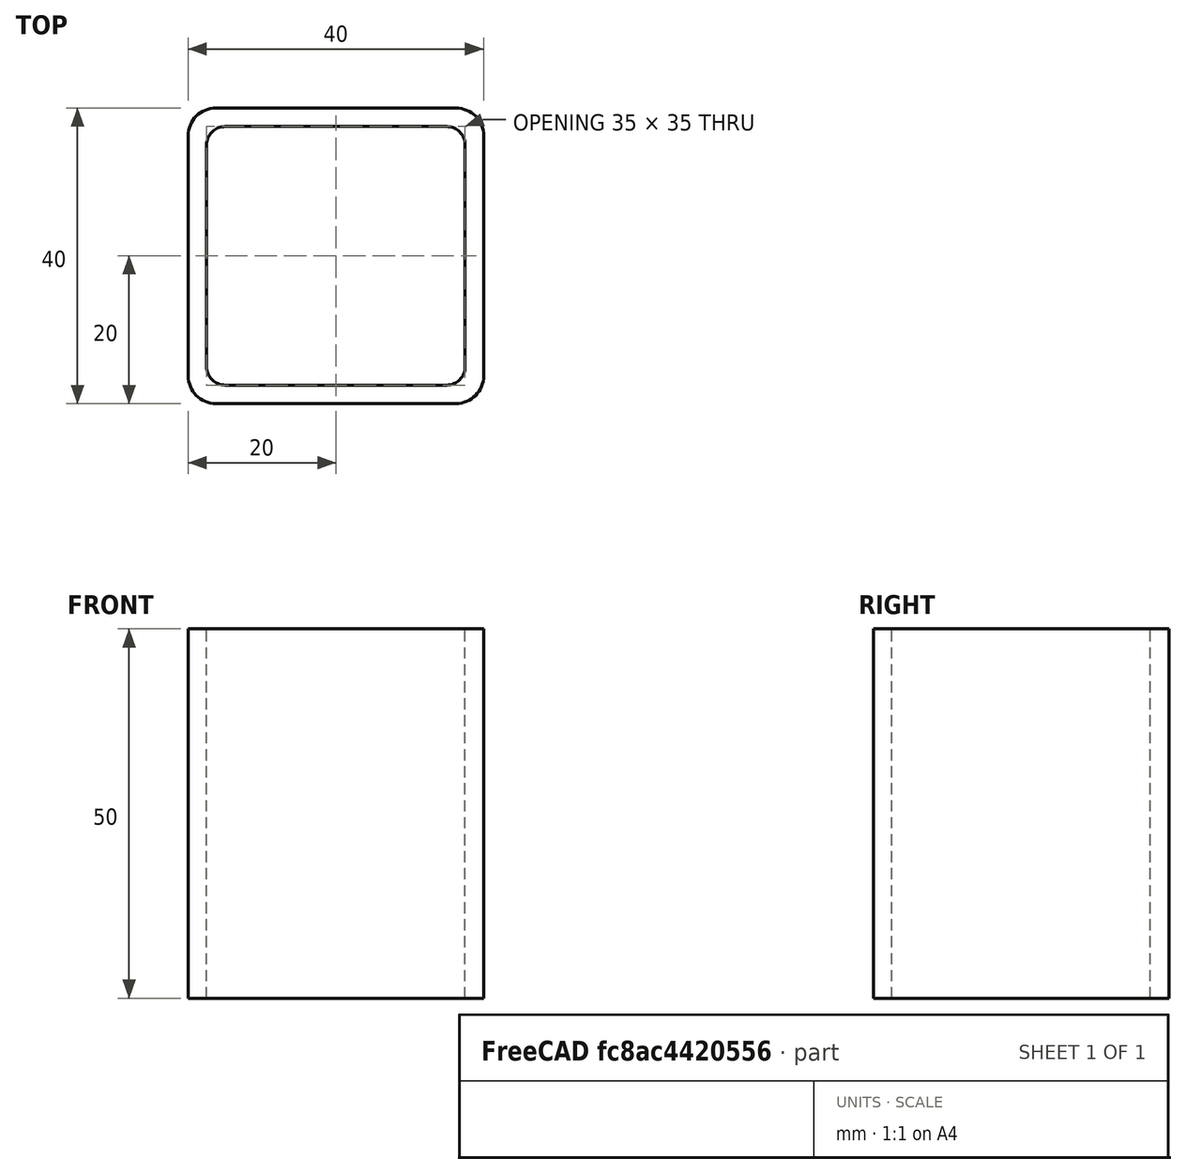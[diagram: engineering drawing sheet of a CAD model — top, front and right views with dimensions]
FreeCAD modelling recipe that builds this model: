
FCSTD DOCUMENT  (FreeCAD 0.15R4671 (Git))
Label: Square hollow section 40x40x2.5 EN10219 S235JRH
License: All rights reserved
LicenseURL: http://en.wikipedia.org/wiki/All_rights_reserved
objects: Sketcher::SketchObject×1, Part::Extrusion×1
note: 2 computed .brp shape members not serialized (recipe doc carries the construction recipe); baked Part::Feature solids carry a one-line shape summary decoded from their .brp

FEATURE [Sketcher::SketchObject] Sketch
  sketch-geometry (16):
    g0: LineSegment StartX=-15 StartY=17.5 StartZ=0 EndX=15 EndY=17.5 EndZ=0
    g1: LineSegment StartX=17.5 StartY=15 StartZ=0 EndX=17.5 EndY=-15 EndZ=0
    g2: LineSegment StartX=15 StartY=-17.5 StartZ=0 EndX=-15 EndY=-17.5 EndZ=0
    g3: LineSegment StartX=-17.5 StartY=-15 StartZ=0 EndX=-17.5 EndY=15 EndZ=0
    g4: LineSegment StartX=-16.25 StartY=20 StartZ=0 EndX=16.25 EndY=20 EndZ=0
    g5: LineSegment StartX=20 StartY=16.25 StartZ=0 EndX=20 EndY=-16.25 EndZ=0
    g6: LineSegment StartX=16.25 StartY=-20 StartZ=0 EndX=-16.25 EndY=-20 EndZ=0
    g7: LineSegment StartX=-20 StartY=-16.25 StartZ=0 EndX=-20 EndY=16.25 EndZ=0
    g8: ArcOfCircle CenterX=-15 CenterY=15 CenterZ=0 NormalX=0 NormalY=0 NormalZ=1 Radius=2.5 StartAngle=1.5708 EndAngle=3.14159
    g9: ArcOfCircle CenterX=15 CenterY=15 CenterZ=0 NormalX=0 NormalY=0 NormalZ=1 Radius=2.5 StartAngle=0 EndAngle=1.5708
    g10: ArcOfCircle CenterX=15 CenterY=-15 CenterZ=0 NormalX=0 NormalY=0 NormalZ=1 Radius=2.5 StartAngle=4.71239 EndAngle=6.28319
    g11: ArcOfCircle CenterX=-15 CenterY=-15 CenterZ=0 NormalX=0 NormalY=0 NormalZ=1 Radius=2.5 StartAngle=3.14159 EndAngle=4.71239
    g12: ArcOfCircle CenterX=16.25 CenterY=16.25 CenterZ=0 NormalX=0 NormalY=0 NormalZ=1 Radius=3.75 StartAngle=0 EndAngle=1.5708
    g13: ArcOfCircle CenterX=16.25 CenterY=-16.25 CenterZ=0 NormalX=0 NormalY=0 NormalZ=1 Radius=3.75 StartAngle=4.71239 EndAngle=6.28319
    g14: ArcOfCircle CenterX=-16.25 CenterY=-16.25 CenterZ=0 NormalX=0 NormalY=0 NormalZ=1 Radius=3.75 StartAngle=3.14159 EndAngle=4.71239
    g15: ArcOfCircle CenterX=-16.25 CenterY=16.25 CenterZ=0 NormalX=0 NormalY=0 NormalZ=1 Radius=3.75 StartAngle=1.5708 EndAngle=3.14159
  constraints (36):
    c: Horizontal(g2)
    c: Vertical(g3)
    c: Horizontal(g6)
    c: Vertical(g7)
    c: Tangent(g3,g8) = 1.5708
    c: Tangent(g0,g8) = 1.5708
    c: Tangent(g0,g9) = 1.5708
    c: Tangent(g1,g9) = 1.5708
    c: Tangent(g1,g10) = 1.5708
    c: Tangent(g2,g10) = 1.5708
    c: Tangent(g2,g11) = 1.5708
    c: Tangent(g3,g11) = 1.5708
    c: Tangent(g4,g12) = 1.5708
    c: Tangent(g5,g12) = 1.5708
    c: Tangent(g5,g13) = 1.5708
    c: Tangent(g6,g13) = 1.5708
    c: Tangent(g6,g14) = 1.5708
    c: Tangent(g7,g14) = 1.5708
    c: Tangent(g7,g15) = 1.5708
    c: Tangent(g4,g15) = 1.5708
    c: Equal(g9,g8)
    c: Equal(g9,g11)
    c: Equal(g9,g10)
    c: Equal(g12,g15)
    c: Equal(g12,g14)
    c: Equal(g12,g13)
    c: Symmetric(g4,g6,g-1)
    c: Symmetric(g7,g5,g-2)
    c: DistanceY(g4,g6) = -40
    c: DistanceX(g7,g5) = 40
    c: Symmetric(g3,g1,g-2)
    c: Symmetric(g0,g2,g-1)
    c: DistanceY(g0,g4) = 2.5
    c: DistanceX(g5,g1) = -2.5
    c: Radius(g9) = 2.5
    c: Radius(g12) = 3.75
FEATURE [Part::Extrusion] Extrude  label="Square hollow section 40x40x2.5 EN10219 S235JRH"
  Base = -> Sketch
  Dir = (0,0,50)
  Solid = true
